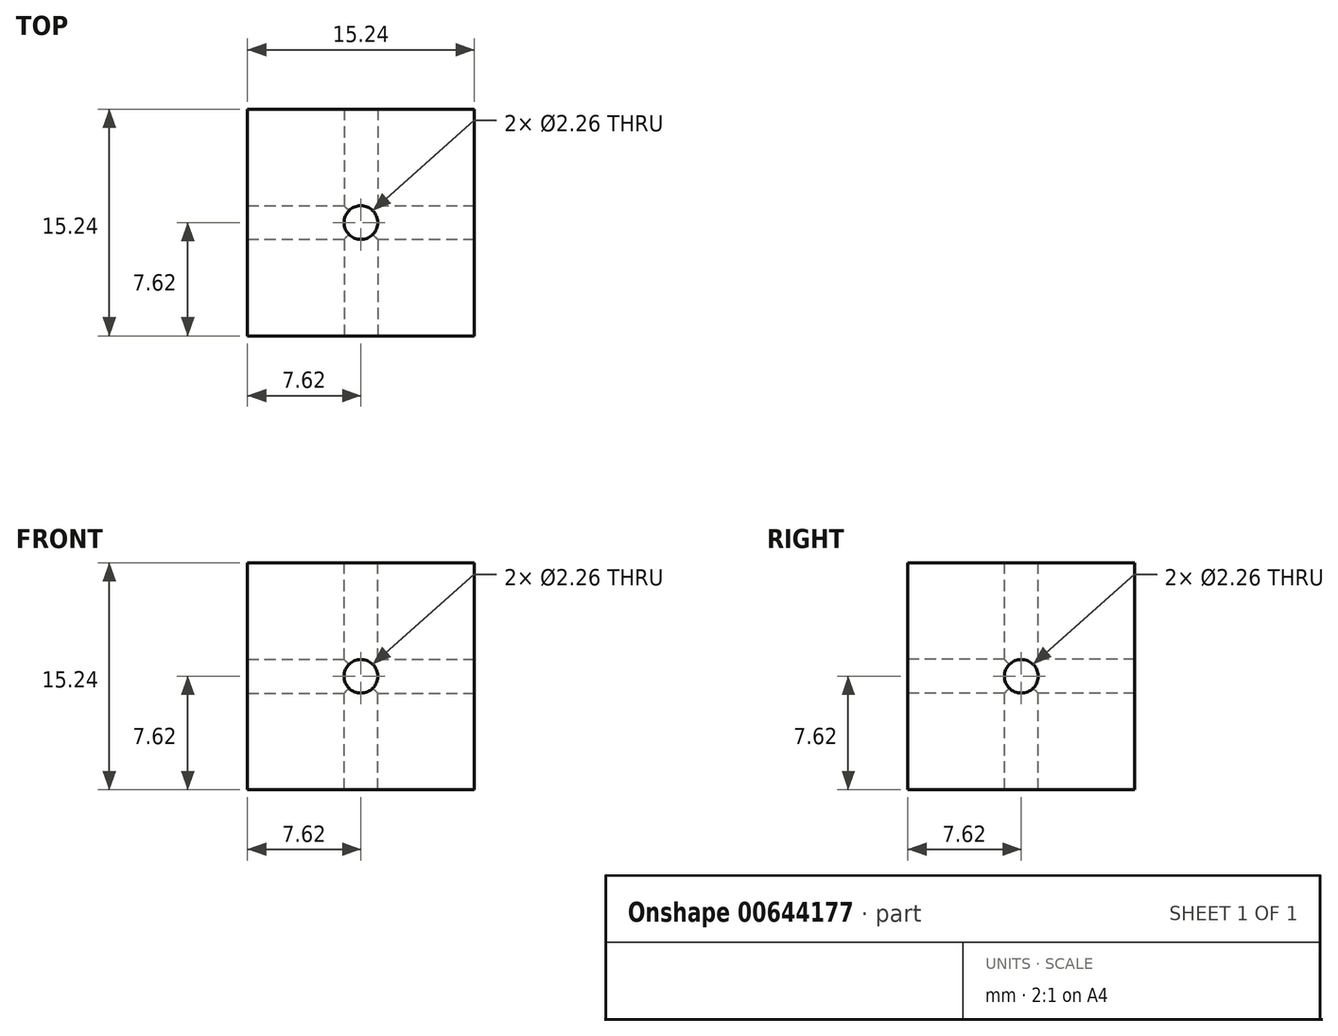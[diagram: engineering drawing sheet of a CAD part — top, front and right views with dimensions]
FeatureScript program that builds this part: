
annotation { "Feature Type Name" : "Feature", "Feature Type Description" : "" }
export const myFeature = defineFeature(function(context is Context, id is Id, definition is map)
    precondition{}
    {
        {
            var Q0;
            Q0=qCreatedBy(makeId("Front.planeOp"),FACE);
            var sketch = newSketch(context, id + "F0", { "sketchPlane" : qUnion([Q0])});
            skLineSegment(sketch, "E0.bottom", {"start": v(0, 0) * mm, "end": v(15.24, 0) * mm});
            skLineSegment(sketch, "E0.top", {"start": v(0, -15.24) * mm, "end": v(15.24, -15.24) * mm});
            skLineSegment(sketch, "E0.left", {"start": v(0, 0) * mm, "end": v(0, -15.24) * mm});
            skLineSegment(sketch, "E0.right", {"start": v(15.24, 0) * mm, "end": v(15.24, -15.24) * mm});
            skSolve(sketch);
        }
        {
            var Q0;
            Q0 = qSketchRegion(id + "F0", true);
            extrude(context, id + "F1", {"entities" : qUnion([Q0]), "depth" : 15.24 * mm, "offsetDistance" : 25.4 * mm});
        }
        {
            var Q0;
            Q0=makeQuery(id+"F1.opExtrude","CAP_FACE",FACE,{"disambiguationData":[OSD([sQuery(id+"F0.wireOp",EDGE,"E0.bottom"),sQuery(id+"F0.wireOp",EDGE,"E0.top"),sQuery(id+"F0.wireOp",EDGE,"E0.left"),sQuery(id+"F0.wireOp",EDGE,"E0.right")])],"isStart":false});
            var sketch = newSketch(context, id + "F2", { "sketchPlane" : qUnion([Q0])});
            skPoint(sketch, "E1", {"position": v(7.62, -7.62) * mm});
            skPoint(sketch, "E1.positionSnap0", {"position": v(15.24, -7.62) * mm});
            skPoint(sketch, "E1.positionSnap1", {"position": v(7.62, -15.24) * mm});
            skSolve(sketch);
        }
        {
            var Q0;
            Q0=makeQuery(id+"F1.opExtrude","SWEPT_FACE",FACE,{"disambiguationData":[OSD([sQuery(id+"F0.wireOp",EDGE,"E0.right")])]});
            var sketch = newSketch(context, id + "F3", { "sketchPlane" : qUnion([Q0])});
            skPoint(sketch, "E2", {"position": v(-7.62, -7.62) * mm});
            skPoint(sketch, "E2.positionSnap0", {"position": v(-7.62, -15.24) * mm});
            skPoint(sketch, "E2.positionSnap1", {"position": v(0, -7.62) * mm});
            skSolve(sketch);
        }
        {
            var Q0;
            Q0=makeQuery(id+"F1.opExtrude","SWEPT_FACE",FACE,{"disambiguationData":[OSD([sQuery(id+"F0.wireOp",EDGE,"E0.bottom")])]});
            var sketch = newSketch(context, id + "F4", { "sketchPlane" : qUnion([Q0])});
            skPoint(sketch, "E3", {"position": v(7.62, -7.62) * mm});
            skPoint(sketch, "E3.positionSnap0", {"position": v(15.24, -7.62) * mm});
            skPoint(sketch, "E3.positionSnap1", {"position": v(7.62, -15.24) * mm});
            skSolve(sketch);
        }
        {
            var Q0;
            Q0=sQuery(id+"F2.wireOp",VERTEX,"E1");
            var Q1;
            Q1=makeQuery(id+"F1.opExtrude","SWEPT_BODY",BODY,{"disambiguationData":[OSD([sQuery(id+"F0.wireOp",EDGE,"E0.bottom"),sQuery(id+"F0.wireOp",EDGE,"E0.top"),sQuery(id+"F0.wireOp",EDGE,"E0.left"),sQuery(id+"F0.wireOp",EDGE,"E0.right")])]});
            hole(context, id + "F5", {"style" : HoleStyle.SIMPLE, "endStyle" : HoleEndStyle.THROUGH, "standardTappedOrClearance" : lookupTablePath({ "standard" : "ANSI", "engagement" : "75%", "pitch" : "40 tpi", "size" : "#4", "type" : "Tapped" }), "standardBlindInLast" : lookupTablePath({ "standard" : "ANSI", "engagement" : "75%", "pitch" : "40 tpi", "size" : "#4", "type" : "Tapped" }), "holeDiameter" : 2.26 * mm, "majorDiameter" : 2.84 * mm, "showTappedDepth" : true, "isTappedThrough" : true, "tappedDepth" : 12.7 * mm, "tapClearance" : 3, "locations" : qUnion([Q0]), "scope" : qUnion([Q1])});
        }
        {
            var Q0;
            Q0=sQuery(id+"F3.wireOp",VERTEX,"E2");
            var Q1;
            Q1=makeQuery(id+"F1.opExtrude","SWEPT_BODY",BODY,{"disambiguationData":[OSD([sQuery(id+"F0.wireOp",EDGE,"E0.bottom"),sQuery(id+"F0.wireOp",EDGE,"E0.top"),sQuery(id+"F0.wireOp",EDGE,"E0.left"),sQuery(id+"F0.wireOp",EDGE,"E0.right")])]});
            hole(context, id + "F6", {"style" : HoleStyle.SIMPLE, "endStyle" : HoleEndStyle.THROUGH, "standardTappedOrClearance" : lookupTablePath({ "standard" : "ANSI", "engagement" : "75%", "pitch" : "40 tpi", "size" : "#4", "type" : "Tapped" }), "standardBlindInLast" : lookupTablePath({ "standard" : "ANSI", "engagement" : "75%", "pitch" : "40 tpi", "size" : "#4", "type" : "Tapped" }), "holeDiameter" : 2.26 * mm, "majorDiameter" : 2.84 * mm, "showTappedDepth" : true, "isTappedThrough" : true, "tappedDepth" : 12.7 * mm, "tapClearance" : 3, "locations" : qUnion([Q0]), "scope" : qUnion([Q1])});
        }
        {
            var Q0;
            Q0=sQuery(id+"F4.wireOp",VERTEX,"E3");
            var Q1;
            Q1=makeQuery(id+"F1.opExtrude","SWEPT_BODY",BODY,{"disambiguationData":[OSD([sQuery(id+"F0.wireOp",EDGE,"E0.bottom"),sQuery(id+"F0.wireOp",EDGE,"E0.top"),sQuery(id+"F0.wireOp",EDGE,"E0.left"),sQuery(id+"F0.wireOp",EDGE,"E0.right")])]});
            hole(context, id + "F7", {"style" : HoleStyle.SIMPLE, "endStyle" : HoleEndStyle.THROUGH, "standardTappedOrClearance" : lookupTablePath({ "standard" : "ANSI", "engagement" : "75%", "pitch" : "40 tpi", "size" : "#4", "type" : "Tapped" }), "standardBlindInLast" : lookupTablePath({ "standard" : "ANSI", "engagement" : "75%", "pitch" : "40 tpi", "size" : "#4", "type" : "Tapped" }), "holeDiameter" : 2.26 * mm, "majorDiameter" : 2.84 * mm, "showTappedDepth" : true, "isTappedThrough" : true, "tappedDepth" : 12.7 * mm, "tapClearance" : 3, "locations" : qUnion([Q0]), "scope" : qUnion([Q1])});
        }
    });
